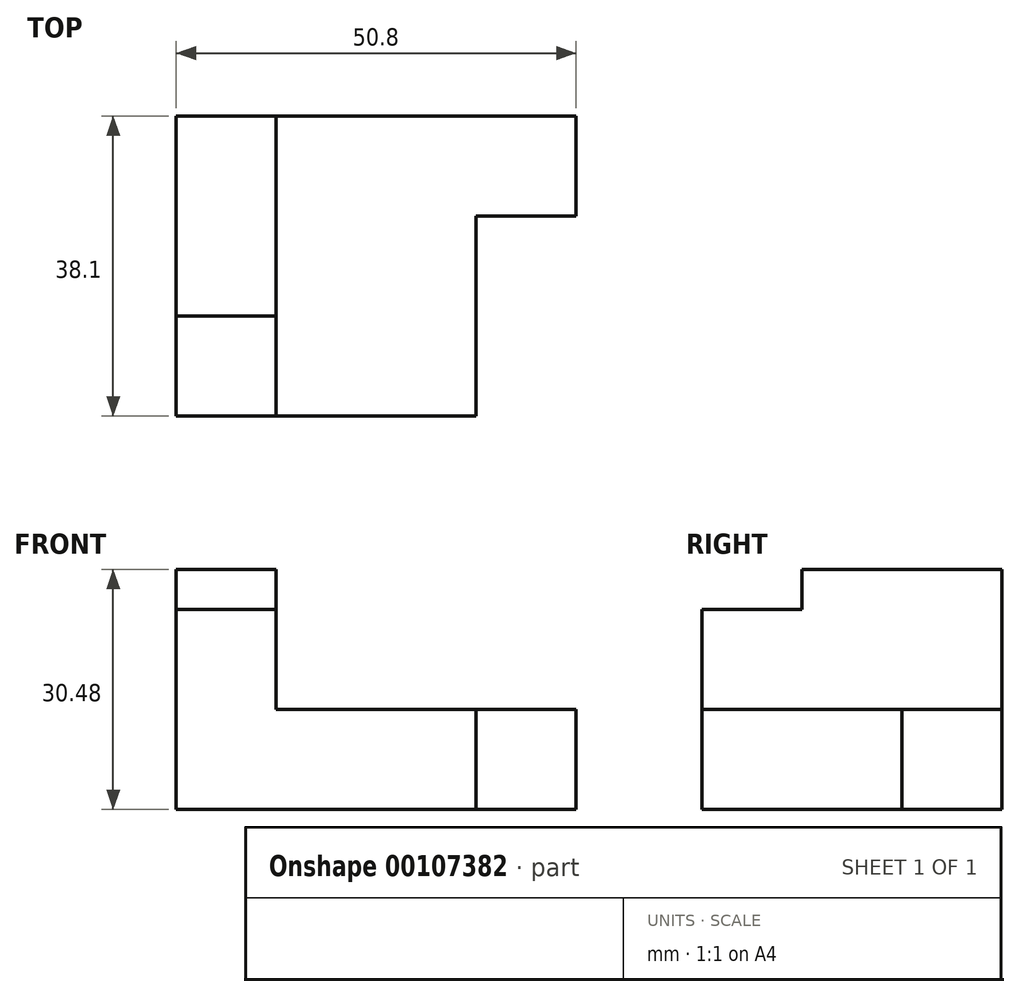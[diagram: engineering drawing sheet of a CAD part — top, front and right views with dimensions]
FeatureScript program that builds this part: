
annotation { "Feature Type Name" : "Feature", "Feature Type Description" : "" }
export const myFeature = defineFeature(function(context is Context, id is Id, definition is map)
    precondition{}
    {
        {
            var Q0;
            Q0=qCreatedBy(makeId("Front.planeOp"),FACE);
            var sketch = newSketch(context, id + "F0", { "sketchPlane" : qUnion([Q0])});
            skLineSegment(sketch, "E0", {"start": v(-77.36, -31.43) * mm, "end": v(-77.36, -0.95) * mm});
            skLineSegment(sketch, "E1", {"start": v(-64.66, -0.95) * mm, "end": v(-77.36, -0.95) * mm});
            skLineSegment(sketch, "E2", {"start": v(-64.66, -0.95) * mm, "end": v(-64.66, -18.73) * mm});
            skLineSegment(sketch, "E3", {"start": v(-64.66, -18.73) * mm, "end": v(-26.56, -18.73) * mm});
            skLineSegment(sketch, "E4", {"start": v(-26.56, -18.73) * mm, "end": v(-26.56, -31.43) * mm});
            skLineSegment(sketch, "E5", {"start": v(-26.56, -31.43) * mm, "end": v(-77.36, -31.43) * mm});
            skSolve(sketch);
        }
        {
            var Q0;
            Q0 = qSketchRegion(id + "F0", true);
            extrude(context, id + "F1", {"entities" : qUnion([Q0]), "depth" : 38.1 * mm});
        }
        {
            var Q0;
            Q0=makeQuery(id+"F1.opExtrude","SWEPT_FACE",FACE,{"disambiguationData":[OSD([sQuery(id+"F0.wireOp",EDGE,"E1")])]});
            var sketch = newSketch(context, id + "F2", { "sketchPlane" : qUnion([Q0])});
            skLineSegment(sketch, "E6", {"start": v(-64.66, -25.4) * mm, "end": v(-64.66, -38.1) * mm});
            skLineSegment(sketch, "E7", {"start": v(-64.66, -38.1) * mm, "end": v(-77.36, -38.1) * mm});
            skLineSegment(sketch, "E8", {"start": v(-77.36, -38.1) * mm, "end": v(-77.36, -25.4) * mm});
            skLineSegment(sketch, "E9", {"start": v(-77.36, -25.4) * mm, "end": v(-64.66, -25.4) * mm});
            skSolve(sketch);
        }
        {
            var Q0;
            Q0 = qSketchRegion(id + "F2", true);
            extrude(context, id + "F3", {"entities" : qUnion([Q0]), "operationType" : NewBodyOperationType.REMOVE, "oppositeDirection" : true, "depth" : 5.08 * mm});
        }
        {
            var Q0;
            Q0=makeQuery(id+"F1.opExtrude","SWEPT_FACE",FACE,{"disambiguationData":[OSD([sQuery(id+"F0.wireOp",EDGE,"E3")])]});
            var sketch = newSketch(context, id + "F4", { "sketchPlane" : qUnion([Q0])});
            skLineSegment(sketch, "E10", {"start": v(-26.56, -12.7) * mm, "end": v(-39.26, -12.7) * mm});
            skLineSegment(sketch, "E11", {"start": v(-39.26, -12.7) * mm, "end": v(-39.26, -38.1) * mm});
            skLineSegment(sketch, "E12", {"start": v(-39.26, -38.1) * mm, "end": v(-26.56, -38.1) * mm});
            skLineSegment(sketch, "E13", {"start": v(-26.56, -38.1) * mm, "end": v(-26.56, -12.7) * mm});
            skSolve(sketch);
        }
        {
            var Q0;
            Q0 = qSketchRegion(id + "F4", true);
            extrude(context, id + "F5", {"entities" : qUnion([Q0]), "operationType" : NewBodyOperationType.REMOVE, "oppositeDirection" : true, "depth" : 12.7 * mm});
        }
    });
